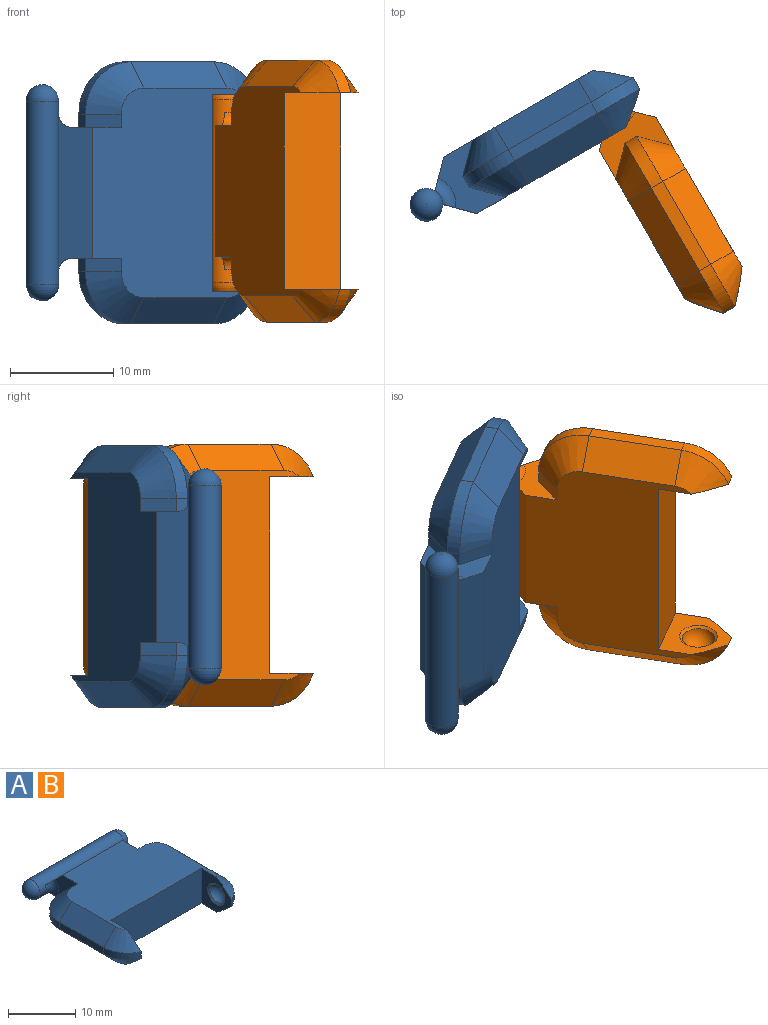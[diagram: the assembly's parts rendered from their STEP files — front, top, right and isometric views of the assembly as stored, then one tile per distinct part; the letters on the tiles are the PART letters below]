
ASSEMBLY  parts=2 mates=1
PART A: 44 faces, bbox 25.5x25.1x6.4 mm
  f0: plane 15.29x2.47mm, normal (0,0.71,-0.71), area 44.1mm2, adj f5,f6,f12,f33,f42,f43
  f1: plane 15.29x2.47mm, normal (0,0.71,0.71), area 44.1mm2, adj f5,f6,f11,f33,f42,f43
  f2: plane 6.35x6.35mm, normal (-1,0,0), area 22.5mm2, adj f10,f11,f12,f13,f17,f29,f40
  f3: plane 9.26x1.27mm, normal (1,0,0), area 11.8mm2, adj f13,f16,f18,f30
  f4: plane 1.27x1.27mm, normal (0,1,0), area 1.6mm2, adj f5,f16,f20,f32
  f5: plane 6.35x4.67mm, normal (1,0,0), area 16.5mm2, adj f0,f1,f4,f11,f12,f20,f32,f42
  f6: plane 6.35x4.67mm, normal (-1,0,0), area 16.5mm2, adj f0,f1,f7,f11,f12,f24,f28,f43
  f7: plane 1.27x1.27mm, normal (0,1,0), area 1.6mm2, adj f6,f15,f24,f28
  f8: plane 9.26x1.27mm, normal (-1,0,0), area 11.8mm2, adj f14,f15,f22,f26
  f9: plane 6.35x6.35mm, normal (1,0,0), area 22.5mm2, adj f10,f11,f12,f14,f21,f25,f41
  f10: plane 19.05x6.35mm, normal (0,-1,0), area 121mm2, adj f2,f9,f11,f12
  f11: plane 20.32x16.66mm, normal (0,0,1), area 247.6mm2, adj f1,f2,f5,f6,f9,f10,f25,f26
  f12: plane 20.32x16.66mm, normal (0,0,-1), area 247.6mm2, adj f0,f2,f5,f6,f9,f10,f17,f18
  f13: cylinder r=5.08mm len=4.71mm, axis (0,0,-1), area 7.7mm2, adj f2,f3,f17,f29
  f14: cylinder r=5.08mm len=4.71mm, axis (0,0,1), area 7.7mm2, adj f8,f9,f21,f25
  f15: cylinder r=5.08mm len=5.08mm, axis (0,0,-1), area 10.1mm2, adj f7,f8,f23,f27
  f16: cylinder r=5.08mm len=5.08mm, axis (0,0,-1), area 10.1mm2, adj f3,f4,f19,f31
  f17: cone r=2.54mm half-angle=45deg, axis (0,0,1), area 14.3mm2, adj f2,f12,f13,f18
  f18: plane 9.26x2.54mm, normal (0.71,0,-0.71), area 33.3mm2, adj f3,f12,f17,f19
  f19: cone r=2.54mm half-angle=45deg, axis (0,0,1), area 21.5mm2, adj f12,f16,f18,f20
  f20: plane 2.54x2.54mm, normal (0,0.71,-0.71), area 4.6mm2, adj f4,f5,f12,f19
  f21: cone r=2.54mm half-angle=45deg, axis (0,0,1), area 14.3mm2, adj f9,f12,f14,f22
  f22: plane 9.26x2.54mm, normal (-0.71,0,-0.71), area 33.3mm2, adj f8,f12,f21,f23
  f23: cone r=2.54mm half-angle=45deg, axis (0,0,1), area 21.5mm2, adj f12,f15,f22,f24
  f24: plane 2.54x2.54mm, normal (0,0.71,-0.71), area 4.6mm2, adj f6,f7,f12,f23
  f25: cone r=2.54mm half-angle=45deg, axis (0,0,-1), area 14.3mm2, adj f9,f11,f14,f26
  f26: plane 9.26x2.54mm, normal (-0.71,0,0.71), area 33.3mm2, adj f8,f11,f25,f27
  f27: cone r=2.54mm half-angle=45deg, axis (0,0,-1), area 21.5mm2, adj f11,f15,f26,f28
  f28: plane 2.54x2.54mm, normal (0,0.71,0.71), area 4.6mm2, adj f6,f7,f11,f27
  f29: cone r=2.54mm half-angle=45deg, axis (0,0,-1), area 14.3mm2, adj f2,f11,f13,f30
  f30: plane 9.26x2.54mm, normal (0.71,0,0.71), area 33.3mm2, adj f3,f11,f29,f31
  f31: cone r=2.54mm half-angle=45deg, axis (0,0,-1), area 21.5mm2, adj f11,f16,f30,f32
  f32: plane 2.54x2.54mm, normal (0,0.71,0.71), area 4.6mm2, adj f4,f5,f11,f31
  f33: cylinder r=1.59mm len=17.78mm, axis (-1,0,0), area 153.2mm2, adj f0,f1,f34,f35,f42,f43
  f34: sphere r=1.59mm, area 15.8mm2, adj f33
  f35: sphere r=1.59mm, area 15.8mm2, adj f33
  f36: plane 0.13x0.13mm, normal (1,0,0), area 0mm2, adj f38
  f37: plane 0.13x0.13mm, normal (-1,0,0), area 0mm2, adj f39
  f38: torus R=0.06mm, axis (1,0,0), area 13.9mm2, adj f36,f41
  f39: torus R=0.06mm, axis (1,0,0), area 13.9mm2, adj f37,f40
  f40: cone r=1.83mm half-angle=48.1deg, axis (-1,0,0), area 3.6mm2, adj f2,f39
  f41: cone r=1.58mm half-angle=48.1deg, axis (1,0,0), area 3.6mm2, adj f9,f38
  f42: torus R=2.86mm, axis (1,0,0), area 4.7mm2, adj f0,f1,f5,f33
  f43: torus R=2.86mm, axis (1,0,0), area 4.7mm2, adj f0,f1,f6,f33
PART B: same geometry as A
PLACE A rot(axis=(0.65,-0.38,0.65),138.6deg) t=(9.65,4.5,9.53)mm
PLACE B rot(axis=(0.25,-0.94,0.25),93.8deg) t=(25.3,-9.93,9.69)mm
MATE cylindrical A.f38 <-> B.f33  axis (0,0,1) through (13.98,3.34,0)mm
